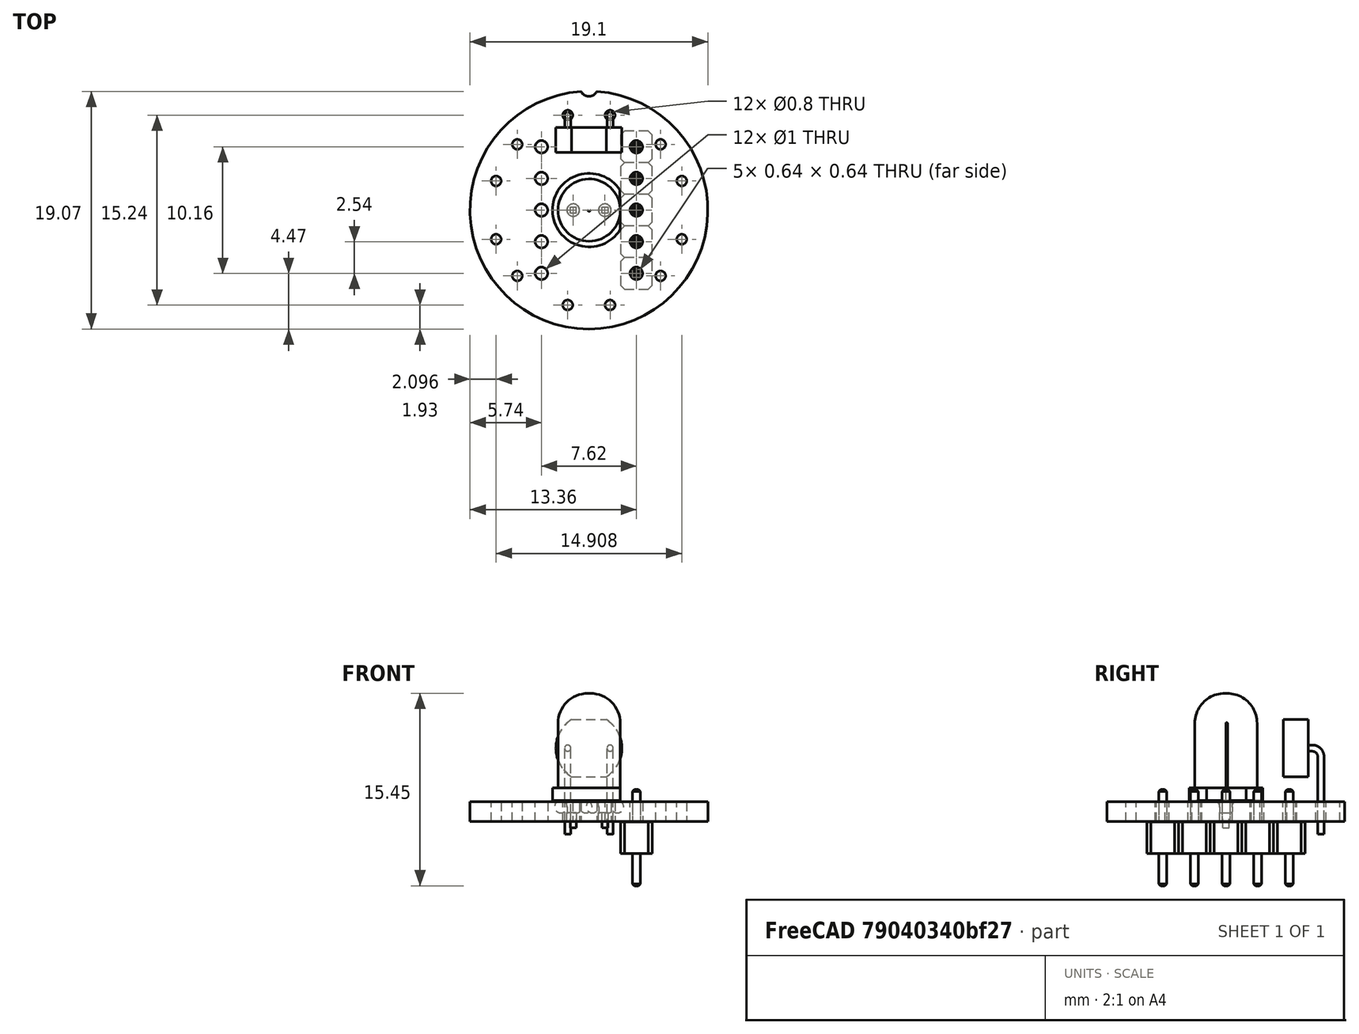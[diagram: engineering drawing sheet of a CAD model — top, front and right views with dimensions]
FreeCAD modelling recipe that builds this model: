
FCSTD DOCUMENT  (FreeCAD 0.19R17089 +1543 (Git))
Label: #200-000 - Photomodule PCB Assembly
License: All rights reserved
LicenseURL: http://en.wikipedia.org/wiki/All_rights_reserved
objects: Part::Feature×6, App::Link×6, App::Part×5, PartDesign::CoordinateSystem×1, Sketcher::SketchObject×1
note: 8 computed .brp shape members not serialized (recipe doc carries the construction recipe); baked Part::Feature solids carry a one-line shape summary decoded from their .brp

FEATURE [PartDesign::CoordinateSystem] Local_CS_9fc9
  AttacherType = Attacher::AttachEngine3D
FEATURE [Part::Feature] Pcb_9fc9
  Placement = pos=(-162.56,93.98,0) rot=(0,0,1;0rad)
  shape: bbox 19.09 x 19.07 x 1.6 mm, 28 faces (baked)
FEATURE [Sketcher::SketchObject] PCB_Sketch_9fc9
  sketch-geometry (2):
    g0: ArcOfCircle CenterX=-1.26931e-10 CenterY=-1.79979e-09 CenterZ=0 NormalX=0 NormalY=0 NormalZ=1 AngleXU=0 Radius=9.54614 StartAngle=1.63736 EndAngle=7.78741
    g1: ArcOfCircle CenterX=1.58877e-11 CenterY=9.8425 CenterZ=0 NormalX=0 NormalY=0 NormalZ=1 AngleXU=0 Radius=0.709952 StartAngle=3.60524 EndAngle=5.81954
  constraints (2):
    c: Coincident(g0,g1)
    c: Coincident(g0,g1)
FEATURE [Part::Feature] Shape  label="D1_Cut_5D8C8806"
  Placement = pos=(0,0,0) rot=(0,0,1;3.14159rad)
  shape: bbox 5.687 x 5.9 x 10.8 mm, 33 faces (baked)
FEATURE [Part::Feature] Shape002  label="LDR6_Waitrony_KE-10720_5D8C8254"
  Placement = pos=(0,7.62,0) rot=(0,0,1;0rad)
  shape: bbox 5.3 x 3.326 x 9.2 mm, 16 faces (baked)
FEATURE [App::Link] LDR6_Waitrony_KE_10720_5D8C8254_ln_  label="LDR5_Waitrony_KE-10720_5D8C8234"
  LinkPlacement = pos=(0,-7.62,0) rot=(0,0,1;3.14159rad)
  LinkedObject = -> Shape002
  Placement = pos=(0,-7.62,0) rot=(0,0,1;3.14159rad)
FEATURE [App::Link] LDR6_Waitrony_KE_10720_5D8C8254_ln_001  label="LDR4_Waitrony_KE-10720_5D8C8214"
  LinkPlacement = pos=(6.604,3.81,0) rot=(0,0,-1;1.0472rad)
  LinkedObject = -> Shape002
  Placement = pos=(6.604,3.81,0) rot=(0,0,-1;1.0472rad)
FEATURE [App::Link] LDR6_Waitrony_KE_10720_5D8C8254_ln_002  label="LDR3_Waitrony_KE-10720_5D8C81F4"
  LinkPlacement = pos=(-6.604,-3.81,0) rot=(0,0,1;2.0944rad)
  LinkedObject = -> Shape002
  Placement = pos=(-6.604,-3.81,0) rot=(0,0,1;2.0944rad)
FEATURE [App::Link] LDR6_Waitrony_KE_10720_5D8C8254_ln_003  label="LDR2_Waitrony_KE-10720_5D8C81D4"
  LinkPlacement = pos=(6.604,-3.81,0) rot=(0,0,1;4.18879rad)
  LinkedObject = -> Shape002
  Placement = pos=(6.604,-3.81,0) rot=(0,0,1;4.18879rad)
FEATURE [App::Link] LDR6_Waitrony_KE_10720_5D8C8254_ln_004  label="LDR1_Waitrony_KE-10720_5D8C81B4"
  LinkPlacement = pos=(-6.604,3.81,0) rot=(0,0,1;1.0472rad)
  LinkedObject = -> Shape002
  Placement = pos=(-6.604,3.81,0) rot=(0,0,1;1.0472rad)
FEATURE [App::Part] Top_9fc9
  Group = -> [Shape,Shape002,LDR6_Waitrony_KE_10720_5D8C8254_ln_,LDR6_Waitrony_KE_10720_5D8C8254_ln_001,LDR6_Waitrony_KE_10720_5D8C8254_ln_002,LDR6_Waitrony_KE_10720_5D8C8254_ln_003,LDR6_Waitrony_KE_10720_5D8C8254_ln_004]
  Origin = -> Origin003
FEATURE [Part::Feature] Shape001  label="J2_Pin_Header_Straight_01x05_ShortPins005_cp_5DBF3AB1"
  Placement = pos=(3.81,5.08,-1.6) rot=(0,1,0;3.14159rad)
  shape: bbox 2.54 x 12.7 x 7.74 mm, 140 faces, 5 solids (baked)
FEATURE [App::Link] J2_Pin_Header_Straight_01x05_ShortPins005_cp_5DBF3AB1_ln_  label="J1_Pin_Header_Straight_01x05_ShortPins005_cp_5DBF3A9E"
  LinkPlacement = pos=(-3.81,5.08,-1.6) rot=(0,1,0;3.14159rad)
  LinkedObject = -> Shape001
  Placement = pos=(-3.81,5.08,-1.6) rot=(0,1,0;3.14159rad)
FEATURE [App::Part] Bot_9fc9
  Group = -> [Shape001,J2_Pin_Header_Straight_01x05_ShortPins005_cp_5DBF3AB1_ln_]
  Origin = -> Origin004
FEATURE [App::Part] Step_Models_9fc9
  Group = -> [Top_9fc9,Bot_9fc9]
  Origin = -> Origin002
FEATURE [Part::Feature] topTracks_9fc9
  Placement = pos=(-162.56,93.98,0.01) rot=(0,0,1;0rad)
  shape: bbox 9.62 x 12.16 x 2e-07 mm, 10 faces, 0 solids (baked)
FEATURE [Part::Feature] botTracks_9fc9
  Placement = pos=(-162.56,93.98,-1.61) rot=(0,0,1;0rad)
  shape: bbox 18.39 x 18.36 x 0.04 mm, 36 faces, 0 solids (baked)
FEATURE [App::Part] Board_Geoms_9fc9
  Group = -> [Local_CS_9fc9,Pcb_9fc9,PCB_Sketch_9fc9,topTracks_9fc9,botTracks_9fc9]
  Origin = -> Origin
FEATURE [App::Part] Board_9fc9  label="#210-000-S1A - Photomodule PCB [LDRs]"
  Group = -> [Board_Geoms_9fc9,Step_Models_9fc9]
  Origin = -> Origin001
